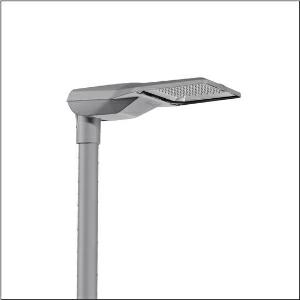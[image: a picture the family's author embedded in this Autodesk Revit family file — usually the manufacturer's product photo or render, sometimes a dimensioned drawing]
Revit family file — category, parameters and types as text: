
# Revit family: streetlight_sl_21_iq_midi___st0_5a_5xe3b31d08nb_970f
name_source: partatom
category: Lighting Fixtures
units: mm (PartAtom-declared; Revit-internal decimal feet)

## family parameters
Cut with Voids When Loaded = No
Host = Face
Light Source = No
Part Type = Normal
Room Calculation Point = No
Round Connector Dimension = Use Diameter
Shared = No

## types (1)
- --- (1 x LED, 23230 lm, 155.5 W, 3000K)
    Apparent Load = 155 VA
    CIE Flux Codes = 43 76 97 100 100
    Color Rendering = 70
    Color Temperature = 3000K
    Default Elevation = 1800 mm
    Description = Streetlight SL 21 iQ midi, mast luminaire, primary light control with lens, of PMMA, primary optical cover: cover, of toughened safety glass, transparent, light distribution: ST0.5a, light emission: direct distribution, primary light characteristic: asymmetric, installation type: post-top, side-entry, LED, High Power LED, rated luminous flux: 23.230lm, luminous efficacy: 149lm/W, light colour: 730, colour temperature: 3000K, control: Auto-Match, Temp-Guard, Lumen-Switch, Night-Set, Smart-Wire, Light-Fading, Desk-Remote (wireless, voltage-free reading and setting of iQ features in the workshop via application-optimized NFC function/RFID function), optimised constant luminous flux control (CLO 2.0), presetting dimming linear, mains connection: 230..240V, AC, 50/60Hz, start of lifetime: 156W, end of service life: 162W, reduction: 69W, luminaire housing, of diecast aluminium, powder-coated, Siteco® metallic grey (DB 702S), corrosivity category C5 mid according to DIN EN ISO 12944, please order mast flange separately, inclination adjustable: 0°, 5°, 10°, 15°, sealing non-destructively replaceable, multi-level sealing system, length: 644mm, width: 335mm, height: 110mm, mast flange for spigot size: 42mm (side-entry): 5XC10008XM4, 60/48mm (side-entry/post-top): 5XC10108XM2, 76/60mm (side-entry/post-top): 5XC10108XM1, protection rating (complete): IP66, insulation class (complete): insulation class II (safety insulation), certification: CE, ENEC, ENEC+, VDE, impact resistance: IK09, permissible operating ambient temperature for outdoor applications: -40..+50°C, standard-compliant lighting for roads and squares, packaging unit: 1 piece

Light Distribution: ST0.5a
    Height = 111 mm
    Lamp = 1 x LED
    Lamp Light Flux = 23230 lm
    Lamp Power = 155.5 W
    Lamp count = 1
    Length = 644 mm
    Luminous efficacy = 149 lm/W
    Manufacturer = Siteco
    ModVariant = No
    Model = 5XE3B31D08NB
    Number of Poles = 1
    OnlyDefault = Yes
    Power Factor = 1
    Product Name = Streetlight SL 21 iQ midi | ST0.5a
    Product group = mast luminaire | pylon top
    ProductGroupID = 6100
    Protection Class = Protection class II
    Protection Degree = IP 66
    RLX_Detail_Level = 1
    RLX_Emergency_Light_Flux = 0 lm
    RLX_Emergency_Type = 0
    RLX_Emergency_Type_DB = No
    RlxData = <blob elided: 102029 chars, md5=c43a090e>
    Socket = socket
    Standby Power = 0 W
    System Light Flux = 23230 lm
    System Power = 155 W
    Type Comments = factory setting: luminous flux: 100 % | dim-lin: 254 | 823 mA
    Type Image = l_1004298.jpg
    URL = http://relux.com
    VarID = @adj_122361
    Voltage = 0 V
    Weight = 0.00 kg
    Width = 336 mm

## geometry (parser evidence)
native form markers: Blend x4, Sweep x11
no freeform markers — native parametric forms only
